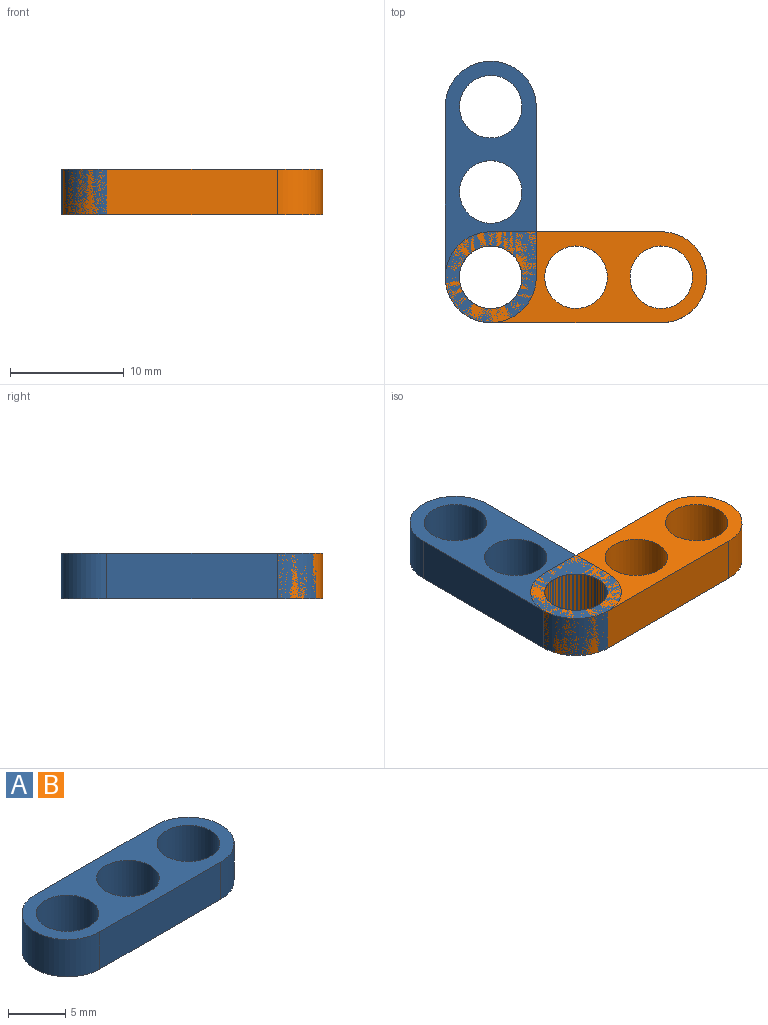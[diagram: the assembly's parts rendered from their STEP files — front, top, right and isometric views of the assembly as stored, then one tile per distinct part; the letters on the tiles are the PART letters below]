
ASSEMBLY  parts=2 mates=1
PART A: 9 faces, bbox 23x8x4 mm
  f0: plane 15x4mm, normal (0,1,0), area 60mm2, adj f1,f5,f7,f8
  f1: cylinder r=4mm len=8mm, axis (0,0,-1), area 50.3mm2, adj f0,f2,f7,f8
  f2: plane 15x4mm, normal (0,-1,0), area 60mm2, adj f1,f5,f7,f8
  f3: cylinder r=2.75mm len=5.5mm, axis (0,0,-1), area 69.1mm2, adj f7,f8
  f4: cylinder r=2.75mm len=5.5mm, axis (0,0,-1), area 69.1mm2, adj f7,f8
  f5: cylinder r=4mm len=8mm, axis (0,0,-1), area 50.3mm2, adj f0,f2,f7,f8
  f6: cylinder r=2.75mm len=5.5mm, axis (0,0,-1), area 69.1mm2, adj f7,f8
  f7: plane 23x8mm, normal (0,0,1), area 99mm2, adj f0,f1,f2,f3,f4,f5,f6
  f8: plane 23x8mm, normal (0,0,-1), area 99mm2, adj f0,f1,f2,f3,f4,f5,f6
PART B: same geometry as A
PLACE A rot(axis=(0,0,1),90deg) t=(6.1,8.1,-6.93)mm
PLACE B rot(axis=(-0.11,0.91,0.39),0deg) t=(6.1,8.1,-6.93)mm
MATE fastened B.f1 <-> A.f1  axis (0,0,1) through (6.1,8.1,-4.93)mm
